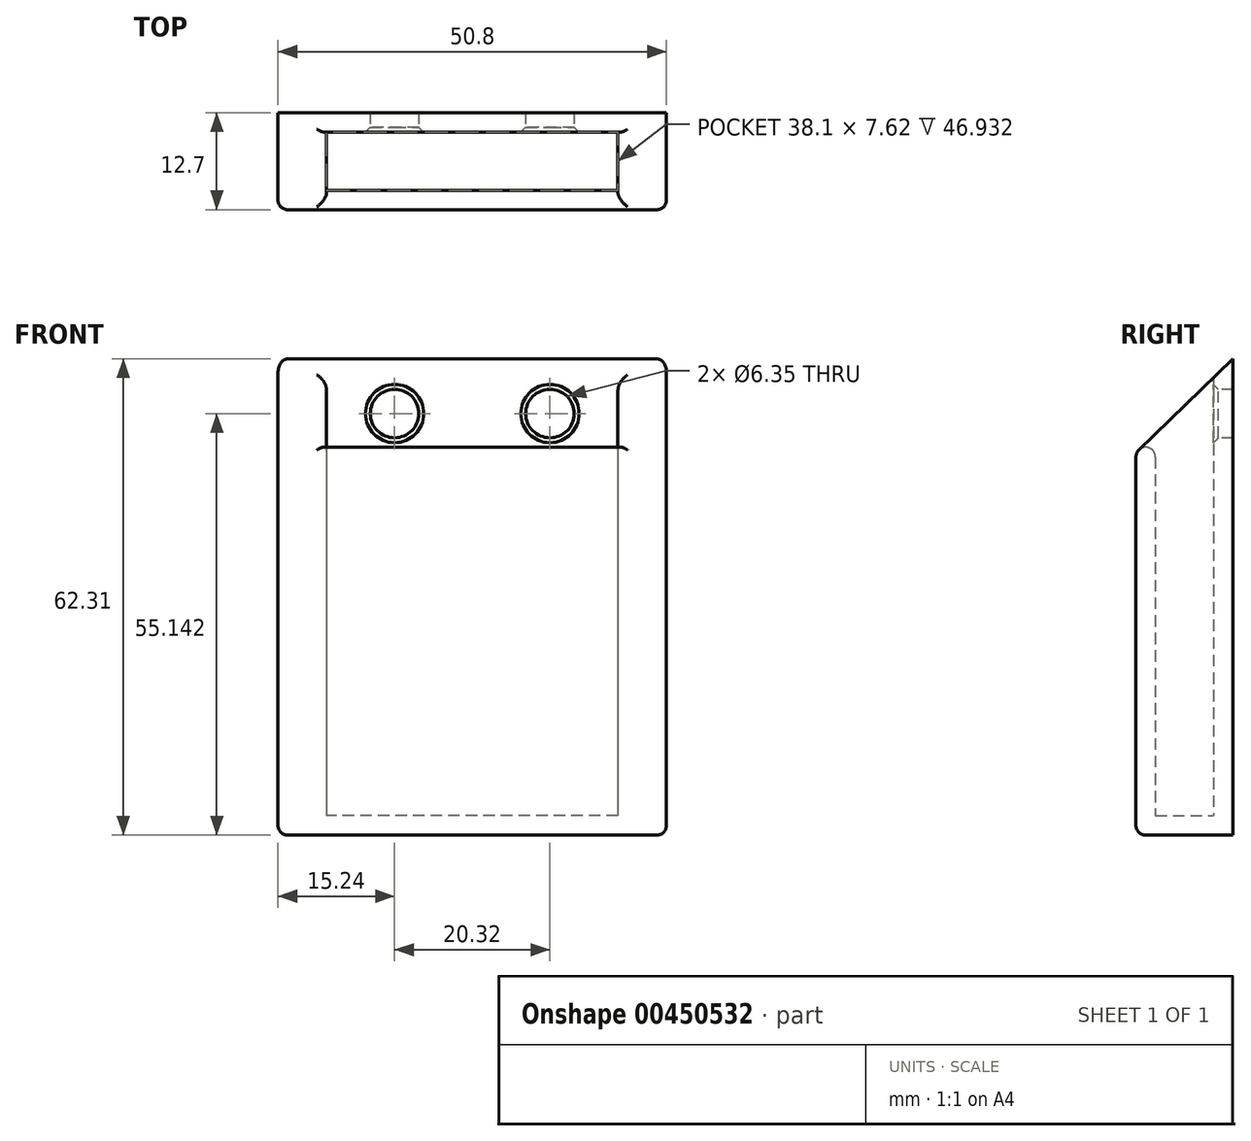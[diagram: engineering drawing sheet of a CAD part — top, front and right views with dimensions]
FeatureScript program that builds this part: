
annotation { "Feature Type Name" : "Feature", "Feature Type Description" : "" }
export const myFeature = defineFeature(function(context is Context, id is Id, definition is map)
    precondition{}
    {
        {
            var Q0;
            Q0=qCreatedBy(makeId("Top.planeOp"),FACE);
            var sketch = newSketch(context, id + "F0", { "sketchPlane" : qUnion([Q0])});
            skLineSegment(sketch, "E0.bottom", {"start": v(25.4, -6.35) * mm, "end": v(-25.4, -6.35) * mm});
            skLineSegment(sketch, "E0.top", {"start": v(25.4, 6.35) * mm, "end": v(-25.4, 6.35) * mm});
            skLineSegment(sketch, "E0.left", {"start": v(25.4, -6.35) * mm, "end": v(25.4, 6.35) * mm});
            skLineSegment(sketch, "E0.right", {"start": v(-25.4, -6.35) * mm, "end": v(-25.4, 6.35) * mm});
            skPoint(sketch, "E0.middle", {"position": v(0, 0) * mm});
            skLineSegment(sketch, "E1.bottom", {"start": v(19.05, -3.8) * mm, "end": v(-19.05, -3.81) * mm});
            skLineSegment(sketch, "E1.top", {"start": v(19.05, 3.81) * mm, "end": v(-19.05, 3.8) * mm});
            skLineSegment(sketch, "E1.left", {"start": v(19.05, -3.8) * mm, "end": v(19.05, 3.81) * mm});
            skLineSegment(sketch, "E1.right", {"start": v(-19.05, -3.81) * mm, "end": v(-19.05, 3.8) * mm});
            skSolve(sketch);
        }
        {
            var Q0;
            Q0=makeQuery(id+"F0.imprint","IMPRINT",FACE,{"disambiguationData":[TD([[makeQuery(id+"F0.imprint","IMPRINT",EDGE,{"derivedFrom":sQuery(id+"F0.wireOp",EDGE,"E0.bottom")}),-1.0]])]});
            var Q1;
            Q1=makeQuery(id+"F0.imprint","IMPRINT",FACE,{"disambiguationData":[TD([[makeQuery(id+"F0.imprint","IMPRINT",EDGE,{"derivedFrom":sQuery(id+"F0.wireOp",EDGE,"E1.bottom")}),-1.0]])]});
            extrude(context, id + "F1", {"entities" : qUnion([Q0, Q1]), "oppositeDirection" : true, "depth" : 2.54 * mm});
        }
        {
            var Q0;
            Q0=makeQuery(id+"F0.imprint","IMPRINT",FACE,{"disambiguationData":[TD([[makeQuery(id+"F0.imprint","IMPRINT",EDGE,{"derivedFrom":sQuery(id+"F0.wireOp",EDGE,"E0.bottom")}),-1.0]])]});
            extrude(context, id + "F2", {"entities" : qUnion([Q0]), "operationType" : NewBodyOperationType.ADD, "depth" : 63.5 * mm});
        }
        {
            var Q0;
            Q0=qCreatedBy(makeId("Right.planeOp"),FACE);
            var sketch = newSketch(context, id + "F3", { "sketchPlane" : qUnion([Q0])});
            skLineSegment(sketch, "E2", {"start": v(-13.94, 40.13) * mm, "end": v(17.33, 70.4) * mm});
            skLineSegment(sketch, "E3", {"start": v(17.33, 70.4) * mm, "end": v(-17.66, 70.4) * mm});
            skLineSegment(sketch, "E4", {"start": v(-17.66, 70.4) * mm, "end": v(-13.94, 40.13) * mm});
            skSolve(sketch);
        }
        {
            var Q0;
            Q0=makeQuery(id+"F3.imprint","IMPRINT",FACE,{"disambiguationData":[TD([[makeQuery(id+"F3.imprint","IMPRINT",EDGE,{"derivedFrom":sQuery(id+"F3.wireOp",EDGE,"E2")}),1.0]])]});
            extrude(context, id + "F4", {"entities" : qUnion([Q0]), "operationType" : NewBodyOperationType.REMOVE, "endBound" : BoundingType.SYMMETRIC, "oppositeDirection" : true, "depth" : 101.6 * mm});
        }
        {
            var Q0;
            {var subQ0=sQuery(id+"F0.wireOp",EDGE,"E0.left");var subQ1=sQuery(id+"F0.wireOp",EDGE,"E0.bottom");Q0=makeQuery(id+"F2.boolean.opBoolean","MERGE",EDGE,{"derivedFrom":[makeQuery(id+"F1.opExtrude","SWEPT_EDGE",EDGE,{"disambiguationData":[OSD([subQ1,subQ0])]}),makeQuery(id+"F2.opExtrude","SWEPT_EDGE",EDGE,{"disambiguationData":[OSD([subQ1,subQ0])]})]});}
            var Q1;
            Q1=makeQuery(id+"F1.opExtrude","CAP_EDGE",EDGE,{"disambiguationData":[OSD([sQuery(id+"F0.wireOp",EDGE,"E0.bottom")])],"isStart":false});
            var Q2;
            Q2=makeQuery(id+"F1.opExtrude","CAP_EDGE",EDGE,{"disambiguationData":[OSD([sQuery(id+"F0.wireOp",EDGE,"E0.left")])],"isStart":false});
            var Q3;
            Q3=makeQuery(id+"F1.opExtrude","CAP_EDGE",EDGE,{"disambiguationData":[OSD([sQuery(id+"F0.wireOp",EDGE,"E0.right")])],"isStart":false});
            var Q4;
            {var subQ0=sQuery(id+"F0.wireOp",EDGE,"E0.right");var subQ1=sQuery(id+"F0.wireOp",EDGE,"E0.bottom");Q4=makeQuery(id+"F2.boolean.opBoolean","MERGE",EDGE,{"derivedFrom":[makeQuery(id+"F1.opExtrude","SWEPT_EDGE",EDGE,{"disambiguationData":[OSD([subQ1,subQ0])]}),makeQuery(id+"F2.opExtrude","SWEPT_EDGE",EDGE,{"disambiguationData":[OSD([subQ1,subQ0])]})]});}
            var Q5;
            {var subQ0=sQuery(id+"F0.wireOp",EDGE,"E0.bottom");Q5=makeQuery(id+"F4.boolean.opBoolean","INTERSECT",EDGE,{"derivedFrom":[makeQuery(id+"F2.boolean.opBoolean","MERGE",FACE,{"derivedFrom":[makeQuery(id+"F1.opExtrude","SWEPT_FACE",FACE,{"disambiguationData":[OSD([subQ0])]}),makeQuery(id+"F2.opExtrude","SWEPT_FACE",FACE,{"disambiguationData":[OSD([subQ0])]})]}),makeQuery(id+"F4.opExtrude","SWEPT_FACE",FACE,{"disambiguationData":[OSD([sQuery(id+"F3.wireOp",EDGE,"E2")])]})]});}
            var Q6;
            Q6=makeQuery(id+"F4.boolean.opBoolean","INTERSECT",EDGE,{"derivedFrom":[makeQuery(id+"F2.opExtrude","SWEPT_FACE",FACE,{"disambiguationData":[OSD([sQuery(id+"F0.wireOp",EDGE,"E1.bottom")])]}),makeQuery(id+"F4.opExtrude","SWEPT_FACE",FACE,{"disambiguationData":[OSD([sQuery(id+"F3.wireOp",EDGE,"E2")])]})]});
            var Q7;
            Q7=makeQuery(id+"F4.boolean.opBoolean","INTERSECT",EDGE,{"derivedFrom":[makeQuery(id+"F2.opExtrude","SWEPT_FACE",FACE,{"disambiguationData":[OSD([sQuery(id+"F0.wireOp",EDGE,"E1.left")])]}),makeQuery(id+"F4.opExtrude","SWEPT_FACE",FACE,{"disambiguationData":[OSD([sQuery(id+"F3.wireOp",EDGE,"E2")])]})]});
            var Q8;
            Q8=makeQuery(id+"F4.boolean.opBoolean","INTERSECT",EDGE,{"derivedFrom":[makeQuery(id+"F2.opExtrude","SWEPT_FACE",FACE,{"disambiguationData":[OSD([sQuery(id+"F0.wireOp",EDGE,"E1.top")])]}),makeQuery(id+"F4.opExtrude","SWEPT_FACE",FACE,{"disambiguationData":[OSD([sQuery(id+"F3.wireOp",EDGE,"E2")])]})]});
            var Q9;
            Q9=makeQuery(id+"F4.boolean.opBoolean","INTERSECT",EDGE,{"derivedFrom":[makeQuery(id+"F2.opExtrude","SWEPT_FACE",FACE,{"disambiguationData":[OSD([sQuery(id+"F0.wireOp",EDGE,"E1.right")])]}),makeQuery(id+"F4.opExtrude","SWEPT_FACE",FACE,{"disambiguationData":[OSD([sQuery(id+"F3.wireOp",EDGE,"E2")])]})]});
            var Q10;
            {var subQ0=sQuery(id+"F0.wireOp",EDGE,"E0.right");Q10=makeQuery(id+"F4.boolean.opBoolean","INTERSECT",EDGE,{"derivedFrom":[makeQuery(id+"F2.boolean.opBoolean","MERGE",FACE,{"derivedFrom":[makeQuery(id+"F1.opExtrude","SWEPT_FACE",FACE,{"disambiguationData":[OSD([subQ0])]}),makeQuery(id+"F2.opExtrude","SWEPT_FACE",FACE,{"disambiguationData":[OSD([subQ0])]})]}),makeQuery(id+"F4.opExtrude","SWEPT_FACE",FACE,{"disambiguationData":[OSD([sQuery(id+"F3.wireOp",EDGE,"E2")])]})]});}
            var Q11;
            {var subQ0=sQuery(id+"F0.wireOp",EDGE,"E0.left");Q11=makeQuery(id+"F4.boolean.opBoolean","INTERSECT",EDGE,{"derivedFrom":[makeQuery(id+"F2.boolean.opBoolean","MERGE",FACE,{"derivedFrom":[makeQuery(id+"F1.opExtrude","SWEPT_FACE",FACE,{"disambiguationData":[OSD([subQ0])]}),makeQuery(id+"F2.opExtrude","SWEPT_FACE",FACE,{"disambiguationData":[OSD([subQ0])]})]}),makeQuery(id+"F4.opExtrude","SWEPT_FACE",FACE,{"disambiguationData":[OSD([sQuery(id+"F3.wireOp",EDGE,"E2")])]})]});}
            fillet(context, id + "F5", {"entities" : qUnion([Q0, Q1, Q2, Q3, Q4, Q5, Q6, Q7, Q8, Q9, Q10, Q11]), "radius" : 1.27 * mm, "tangentPropagation" : true, "allowEdgeOverflow" : false});
        }
        {
            var Q0;
            Q0=qCreatedBy(makeId("Front.planeOp"),FACE);
            var sketch = newSketch(context, id + "F6", { "sketchPlane" : qUnion([Q0])});
            skCircle(sketch, "E5", {"center": v(-10.16, 52.6) * mm, "radius": 3.18 * mm});
            skCircle(sketch, "E6.MirrorC", {"center": v(10.16, 52.6) * mm, "radius": 3.18 * mm});
            skSolve(sketch);
        }
        {
            var Q0;
            Q0 = qSketchRegion(id + "F6", true);
            extrude(context, id + "F7", {"entities" : qUnion([Q0]), "operationType" : NewBodyOperationType.REMOVE, "endBound" : BoundingType.SYMMETRIC, "oppositeDirection" : true, "depth" : 25.4 * mm});
        }
        {
            var Q0;
            Q0=makeQuery(id+"F7.boolean.opBoolean","INTERSECT",EDGE,{"derivedFrom":[makeQuery(id+"F2.opExtrude","SWEPT_FACE",FACE,{"disambiguationData":[OSD([sQuery(id+"F0.wireOp",EDGE,"E1.top")])]}),makeQuery(id+"F7.opExtrude","SWEPT_FACE",FACE,{"disambiguationData":[OSD([sQuery(id+"F6.wireOp",EDGE,"E5")])]})]});
            var Q1;
            Q1=makeQuery(id+"F7.boolean.opBoolean","INTERSECT",EDGE,{"derivedFrom":[makeQuery(id+"F2.opExtrude","SWEPT_FACE",FACE,{"disambiguationData":[OSD([sQuery(id+"F0.wireOp",EDGE,"E1.top")])]}),makeQuery(id+"F7.opExtrude","SWEPT_FACE",FACE,{"disambiguationData":[OSD([sQuery(id+"F6.wireOp",EDGE,"E6.MirrorC")])]})]});
            chamfer(context, id + "F8", {"entities" : qUnion([Q0, Q1]), "width" : 0.64 * mm, "tangentPropagation" : true});
        }
    });
